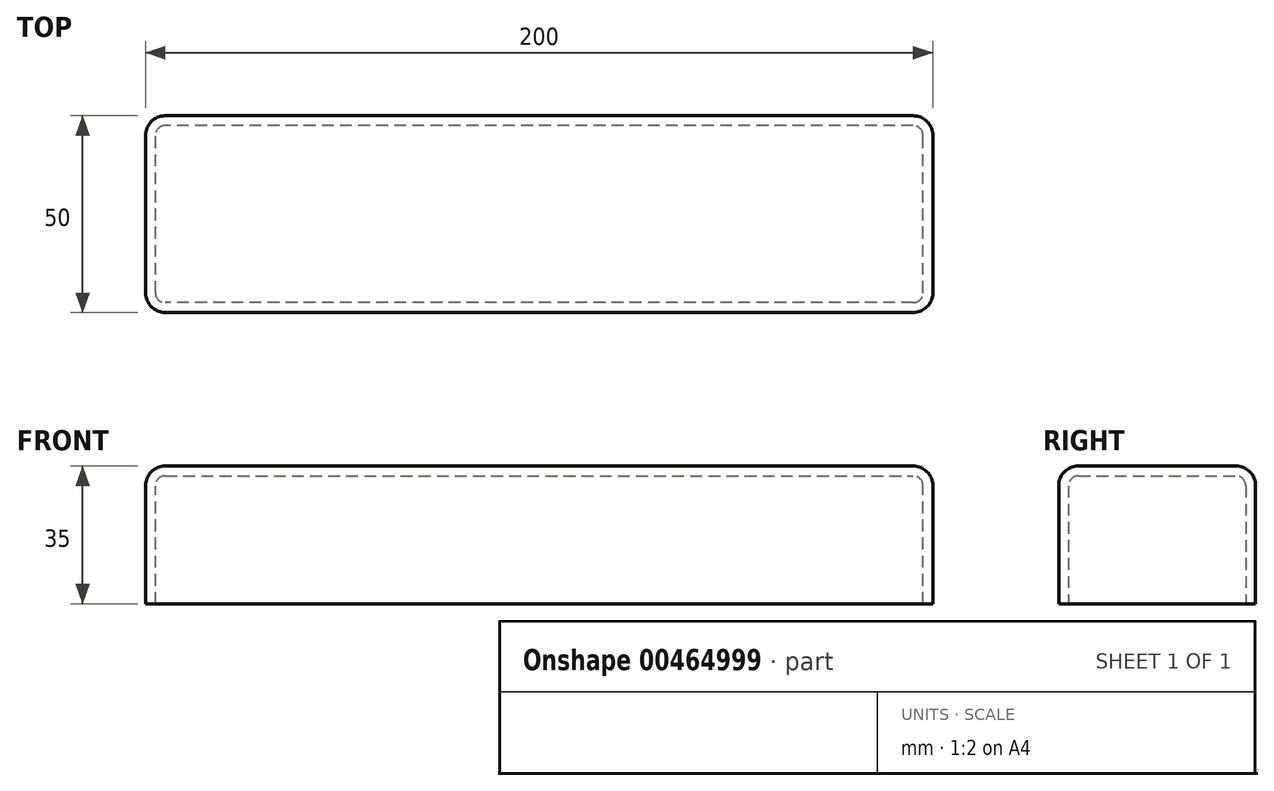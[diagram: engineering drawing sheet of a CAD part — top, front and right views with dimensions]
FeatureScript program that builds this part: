
annotation { "Feature Type Name" : "Feature", "Feature Type Description" : "" }
export const myFeature = defineFeature(function(context is Context, id is Id, definition is map)
    precondition{}
    {
        {
            var Q0;
            Q0=qCreatedBy(makeId("Top.planeOp"),FACE);
            var sketch = newSketch(context, id + "F0", { "sketchPlane" : qUnion([Q0])});
            skLineSegment(sketch, "E0.bottom", {"start": v(0, 0) * mm, "end": v(-200, 0) * mm});
            skLineSegment(sketch, "E0.top", {"start": v(0, 50) * mm, "end": v(-200, 50) * mm});
            skLineSegment(sketch, "E0.left", {"start": v(0, 0) * mm, "end": v(0, 50) * mm});
            skLineSegment(sketch, "E0.right", {"start": v(-200, 0) * mm, "end": v(-200, 50) * mm});
            skSolve(sketch);
        }
        {
            var Q0;
            Q0 = qSketchRegion(id + "F0", true);
            extrude(context, id + "F1", {"entities" : qUnion([Q0]), "depth" : 35 * mm});
        }
        {
            var Q0;
            Q0=makeQuery(id+"F1.opExtrude","SWEPT_EDGE",EDGE,{"disambiguationData":[OSD([sQuery(id+"F0.wireOp",EDGE,"E0.bottom"),sQuery(id+"F0.wireOp",EDGE,"E0.left")])]});
            var Q1;
            Q1=makeQuery(id+"F1.opExtrude","CAP_EDGE",EDGE,{"disambiguationData":[OSD([sQuery(id+"F0.wireOp",EDGE,"E0.left")])],"isStart":false});
            var Q2;
            Q2=makeQuery(id+"F1.opExtrude","SWEPT_EDGE",EDGE,{"disambiguationData":[OSD([sQuery(id+"F0.wireOp",EDGE,"E0.top"),sQuery(id+"F0.wireOp",EDGE,"E0.left")])]});
            var Q3;
            Q3=makeQuery(id+"F1.opExtrude","CAP_EDGE",EDGE,{"disambiguationData":[OSD([sQuery(id+"F0.wireOp",EDGE,"E0.top")])],"isStart":false});
            var Q4;
            Q4=makeQuery(id+"F1.opExtrude","CAP_EDGE",EDGE,{"disambiguationData":[OSD([sQuery(id+"F0.wireOp",EDGE,"E0.bottom")])],"isStart":false});
            var Q5;
            Q5=makeQuery(id+"F1.opExtrude","SWEPT_EDGE",EDGE,{"disambiguationData":[OSD([sQuery(id+"F0.wireOp",EDGE,"E0.bottom"),sQuery(id+"F0.wireOp",EDGE,"E0.right")])]});
            var Q6;
            Q6=makeQuery(id+"F1.opExtrude","CAP_EDGE",EDGE,{"disambiguationData":[OSD([sQuery(id+"F0.wireOp",EDGE,"E0.right")])],"isStart":false});
            var Q7;
            Q7=makeQuery(id+"F1.opExtrude","SWEPT_EDGE",EDGE,{"disambiguationData":[OSD([sQuery(id+"F0.wireOp",EDGE,"E0.top"),sQuery(id+"F0.wireOp",EDGE,"E0.right")])]});
            fillet(context, id + "F2", {"entities" : qUnion([Q0, Q1, Q2, Q3, Q4, Q5, Q6, Q7]), "radius" : 5 * mm, "tangentPropagation" : true, "allowEdgeOverflow" : false});
        }
        {
            var Q0;
            Q0=makeQuery(id+"F1.opExtrude","CAP_FACE",FACE,{"disambiguationData":[OSD([sQuery(id+"F0.wireOp",EDGE,"E0.bottom"),sQuery(id+"F0.wireOp",EDGE,"E0.top"),sQuery(id+"F0.wireOp",EDGE,"E0.left"),sQuery(id+"F0.wireOp",EDGE,"E0.right")])],"isStart":true});
            shell(context, id + "F3", {"entities" : qUnion([Q0]), "thickness" : 2.5 * mm});
        }
    });
